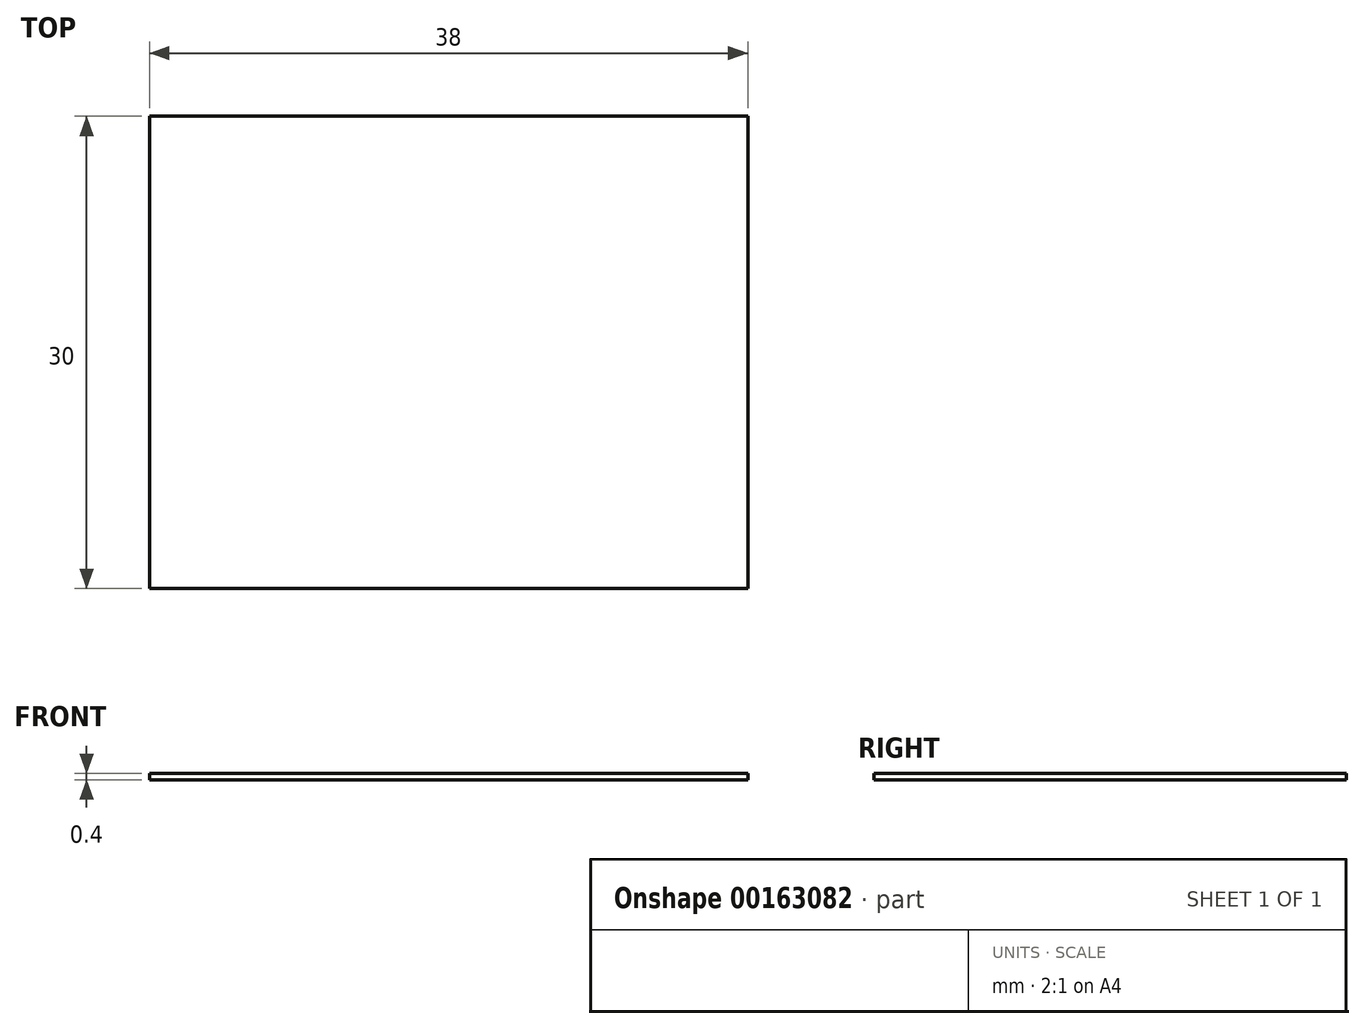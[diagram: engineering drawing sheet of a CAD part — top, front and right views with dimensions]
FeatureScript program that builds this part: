
annotation { "Feature Type Name" : "Feature", "Feature Type Description" : "" }
export const myFeature = defineFeature(function(context is Context, id is Id, definition is map)
    precondition{}
    {
        {
            var Q0;
            Q0=qCreatedBy(makeId("Top.planeOp"),FACE);
            var sketch = newSketch(context, id + "F0", { "sketchPlane" : qUnion([Q0])});
            skLineSegment(sketch, "E0.bottom", {"start": v(19, -15) * mm, "end": v(-19, -15) * mm});
            skLineSegment(sketch, "E0.top", {"start": v(19, 15) * mm, "end": v(-19, 15) * mm});
            skLineSegment(sketch, "E0.left", {"start": v(19, -15) * mm, "end": v(19, 15) * mm});
            skLineSegment(sketch, "E0.right", {"start": v(-19, -15) * mm, "end": v(-19, 15) * mm});
            skPoint(sketch, "E0.middle", {"position": v(0, 0) * mm});
            skSolve(sketch);
        }
        {
            var Q0;
            Q0=makeQuery(id+"F0.imprint","IMPRINT",FACE,{"disambiguationData":[TD([[makeQuery(id+"F0.imprint","IMPRINT",EDGE,{"derivedFrom":sQuery(id+"F0.wireOp",EDGE,"cS4E7c7k-azQk-FOjN-nh0I-Kpbb8iskPe8u")}),-1.0]])]});
            var Q1;
            Q1=makeQuery(id+"F0.imprint","IMPRINT",FACE,{"disambiguationData":[TD([[makeQuery(id+"F0.imprint","IMPRINT",EDGE,{"derivedFrom":sQuery(id+"F0.wireOp",EDGE,"E0.bottom")}),-1.0]])]});
            extrude(context, id + "F1", {"entities" : qUnion([Q0, Q1]), "depth" : .4 * mm});
        }
    });
